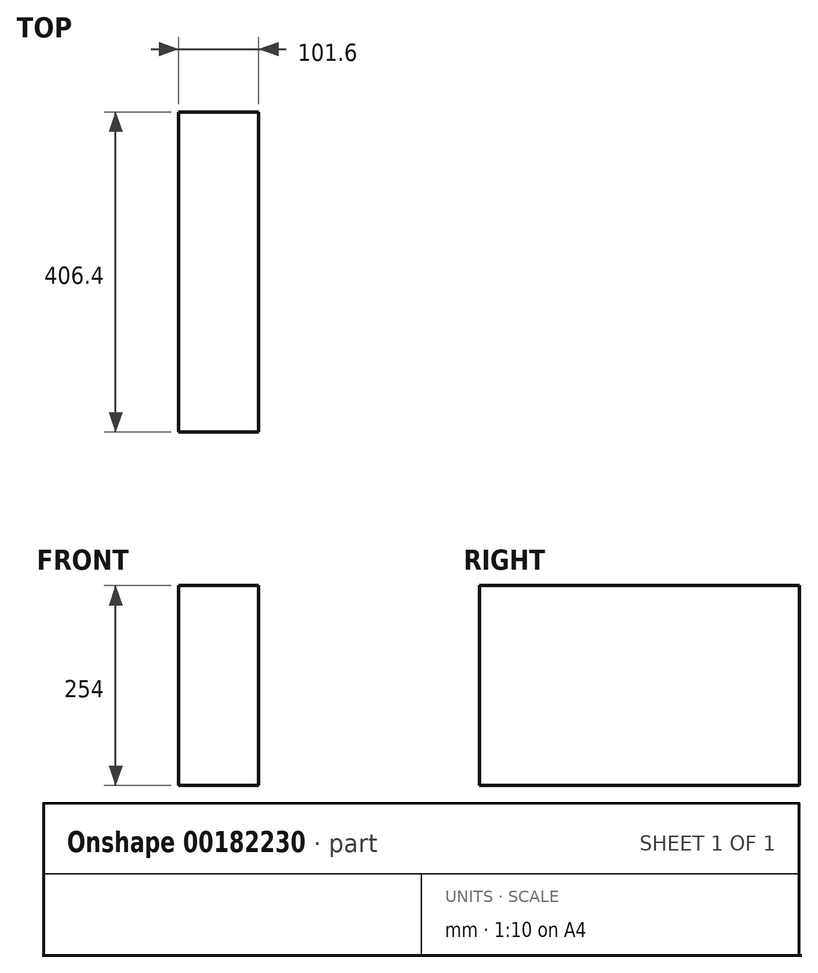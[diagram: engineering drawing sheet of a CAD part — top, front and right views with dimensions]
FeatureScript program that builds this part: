
annotation { "Feature Type Name" : "Feature", "Feature Type Description" : "" }
export const myFeature = defineFeature(function(context is Context, id is Id, definition is map)
    precondition{}
    {
        {
            var Q0;
            Q0=qCreatedBy(makeId("Front.planeOp"),FACE);
            var sketch = newSketch(context, id + "F0", { "sketchPlane" : qUnion([Q0])});
            skLineSegment(sketch, "E0.bottom", {"start": v(0, 0) * mm, "end": v(101.6, 0) * mm});
            skLineSegment(sketch, "E0.top", {"start": v(0, 254) * mm, "end": v(101.6, 254) * mm});
            skLineSegment(sketch, "E0.left", {"start": v(0, 0) * mm, "end": v(0, 254) * mm});
            skLineSegment(sketch, "E0.right", {"start": v(101.6, 0) * mm, "end": v(101.6, 254) * mm});
            skSolve(sketch);
        }
        {
            var Q0;
            Q0=makeQuery(id+"F0.imprint","IMPRINT",FACE,{"disambiguationData":[TD([[makeQuery(id+"F0.imprint","IMPRINT",EDGE,{"derivedFrom":sQuery(id+"F0.wireOp",EDGE,"E0.bottom")}),1.0]])]});
            extrude(context, id + "F1", {"entities" : qUnion([Q0]), "oppositeDirection" : true, "depth" : 406.4 * mm});
        }
    });
